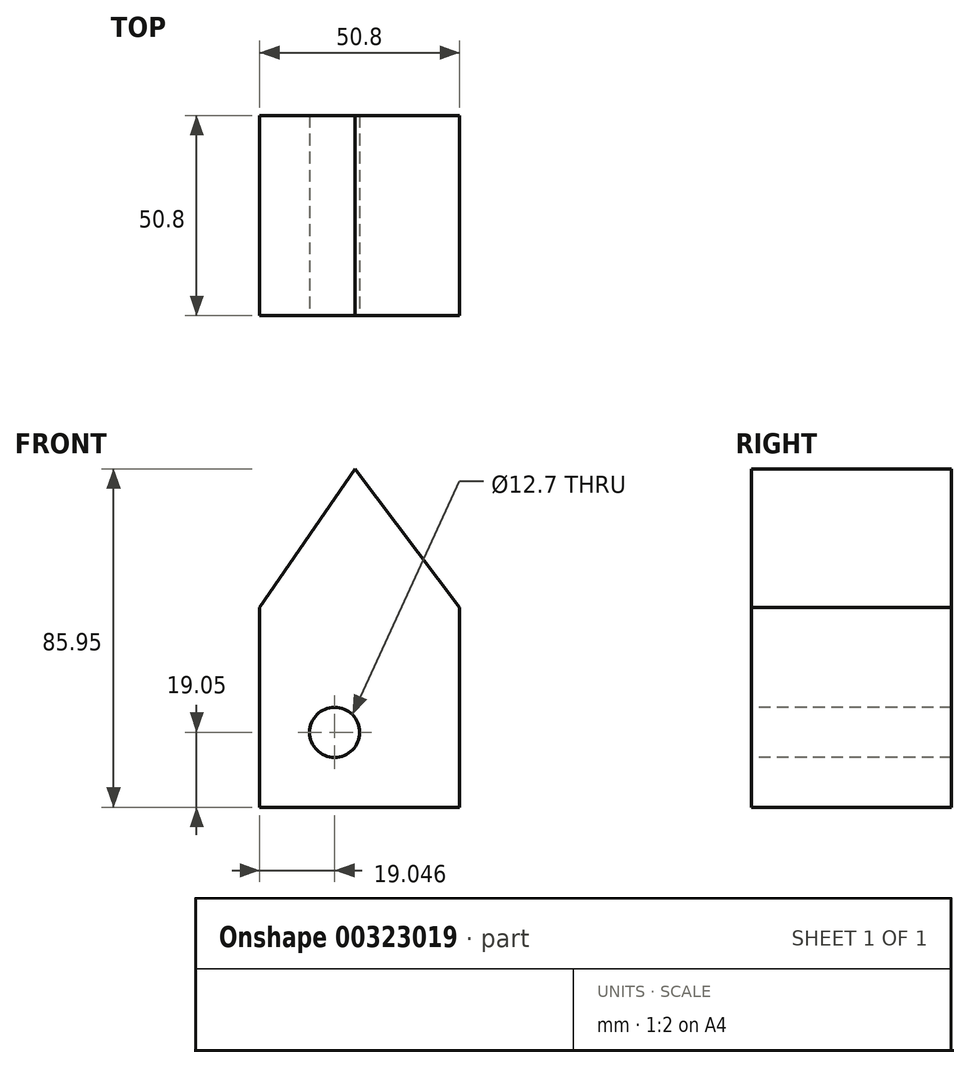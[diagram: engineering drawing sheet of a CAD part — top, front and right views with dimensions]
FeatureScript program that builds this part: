
annotation { "Feature Type Name" : "Feature", "Feature Type Description" : "" }
export const myFeature = defineFeature(function(context is Context, id is Id, definition is map)
    precondition{}
    {
        {
            var Q0;
            Q0=qCreatedBy(makeId("Front.planeOp"),FACE);
            var sketch = newSketch(context, id + "F0", { "sketchPlane" : qUnion([Q0])});
            skLineSegment(sketch, "E0.bottom", {"start": v(-134.72, -4.42) * mm, "end": v(-134.72, -4.42) * mm});
            skLineSegment(sketch, "E0.top", {"start": v(-134.72, -8.69) * mm, "end": v(-134.72, -8.69) * mm});
            skLineSegment(sketch, "E0.left", {"start": v(-134.72, -4.42) * mm, "end": v(-134.72, -8.69) * mm});
            skLineSegment(sketch, "E0.right", {"start": v(-134.72, -4.42) * mm, "end": v(-134.72, -8.69) * mm});
            skPoint(sketch, "E0.middle", {"position": v(-134.72, -6.55) * mm});
            skLineSegment(sketch, "E1.top", {"start": v(-14.83, -33.68) * mm, "end": v(35.97, -33.68) * mm});
            skLineSegment(sketch, "E1.left", {"start": v(-14.83, 17.12) * mm, "end": v(-14.83, -33.68) * mm});
            skLineSegment(sketch, "E1.right", {"start": v(35.97, 17.12) * mm, "end": v(35.97, -33.68) * mm});
            skLineSegment(sketch, "E2", {"start": v(-14.83, 17.12) * mm, "end": v(14.04, 58.92) * mm});
            skLineSegment(sketch, "E3", {"start": v(5.37, 57.68) * mm, "end": v(35.97, 17.12) * mm});
            skCircle(sketch, "E4", {"center": v(4.22, -14.63) * mm, "radius": 6.35 * mm});
            skSolve(sketch);
        }
        {
            var Q0;
            Q0 = qSketchRegion(id + "F0", true);
            extrude(context, id + "F1", {"entities" : qUnion([Q0]), "oppositeDirection" : true, "depth" : 50.8 * mm});
        }
    });
